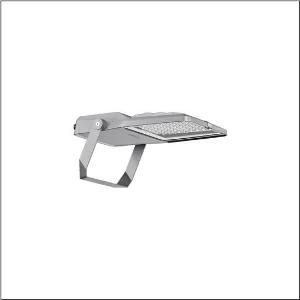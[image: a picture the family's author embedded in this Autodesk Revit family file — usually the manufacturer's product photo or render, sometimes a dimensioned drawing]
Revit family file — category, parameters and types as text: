
# Revit family: floodlight_fl_21_iq_mini___pl64_5xa7772d4e1a_07d3
name_source: partatom
category: Lighting Fixtures
units: mm (PartAtom-declared; Revit-internal decimal feet)

## family parameters
Cut with Voids When Loaded = No
Host = Face
Light Source = No
Part Type = Normal
Room Calculation Point = No
Round Connector Dimension = Use Diameter
Shared = No

## types (1)
- --- (1 x LED, 17970 lm, 143 W, 4000K)
    Apparent Load = 143 VA
    CIE Flux Codes = 28 80 98 100 100
    Color Rendering = 70
    Color Temperature = 4000K
    Default Elevation = 1800 mm
    Description = Floodlight FL 21 iQ mini, floodlight, primary light control with lens, of PMMA, primary optical cover: protective disc, of toughened safety glass, transparent, light distribution: PL64, light emission: direct distribution, installation type: surface-mounted, LED, High Power LED, rated luminous flux: 17.970lm, luminous efficacy: 126lm/W, light colour: 740, colour temperature: 4000K, control: Street-Remote, Auto-Match, Temp-Guard, Night-Set, Smart-Wire, Desk-Remote (wireless, voltage-free reading and setting of iQ features in the workshop via application-optimized NFC function/RFID function), optimised constant luminous flux control (CLO 2.0), with terminal, 6-pole, mains connection: 220..240V, AC, 50/60Hz, start of lifetime: 143W, end of service life: 152W, reduction: 61W, luminaire housing, of diecast aluminium, powder-coated, Siteco® metallic grey (DB 702S), corrosivity category C5 mid according to DIN EN ISO 12944, sealing non-destructively replaceable, mounting bracket, of steel, galvanised, powder-coated, Siteco® metallic grey (DB 702S), protection rating (complete): IP66, insulation class (complete): insulation class II (safety insulation), certification: CE, ENEC, VDE, protection symbol: D, impact resistance: IK08, permissible operating ambient temperature: -40..+40°C, permissible operating ambient temperature for outdoor applications: -40..+50°C, standard: DIN EN 12944, LABS conformity tested according to VDMA 24364:2018-05, packaging unit: 1 piece

Light Distribution: PL64
    Height = 70 mm
    Lamp = 1 x LED
    Lamp Light Flux = 17970 lm
    Lamp Power = 143 W
    Lamp count = 1
    Length = 485 mm
    Luminous efficacy = 126 lm/W
    Manufacturer = Siteco
    ModVariant = No
    Model = 5XA7772D4E1A
    Number of Poles = 1
    OnlyDefault = Yes
    Power Factor = 1
    Product Name = Floodlight FL 21 iQ mini | PL64
    Product group = floodlight | pylon annexe
    ProductGroupID = 6200
    Protection Class = Protection class II
    Protection Degree = IP 66
    RLX_Detail_Level = 1
    RLX_Emergency_Light_Flux = 0 lm
    RLX_Emergency_Type = 0
    RLX_Emergency_Type_DB = No
    RlxData = <blob elided: 96665 chars, md5=d134427a>
    Socket = socket
    Standby Power = 0 W
    System Light Flux = 17970 lm
    System Power = 143 W
    Type Comments = factory setting: luminous flux: 100 % | dim-lin: 254 | 730 mA
    Type Image = l_1006845.jpg
    URL = http://relux.com
    VarID = @adj_098025
    Voltage = 0 V
    Weight = 0.00 kg
    Width = 337 mm

## geometry (parser evidence)
native form markers: Blend x4, Sweep x13
no freeform markers — native parametric forms only
